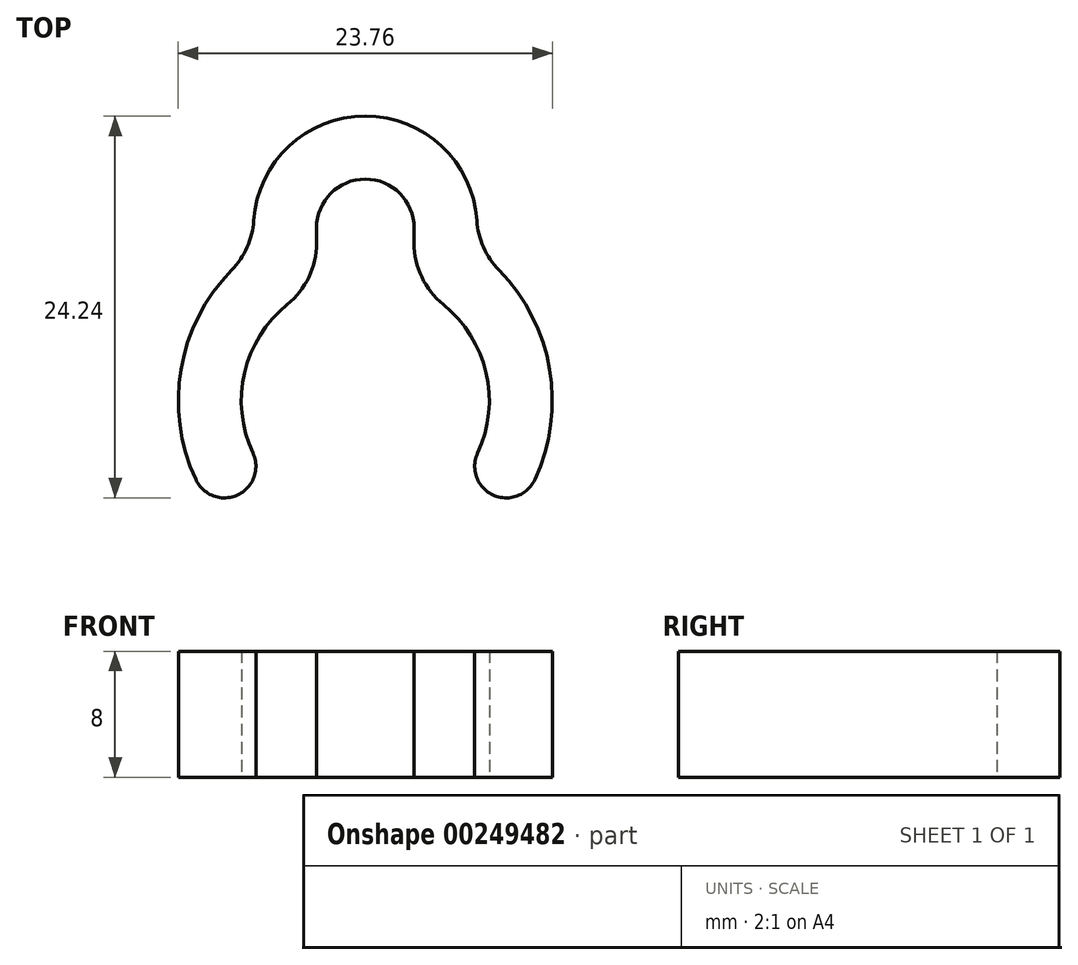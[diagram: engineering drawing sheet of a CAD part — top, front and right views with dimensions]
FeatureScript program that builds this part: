
annotation { "Feature Type Name" : "Feature", "Feature Type Description" : "" }
export const myFeature = defineFeature(function(context is Context, id is Id, definition is map)
    precondition{}
    {
        {
            var Q0;
            Q0=qCreatedBy(makeId("Top.planeOp"),FACE);
            var sketch = newSketch(context, id + "F0", { "sketchPlane" : qUnion([Q0])});
            skCircle(sketch, "E0", {"center": v(0, 0) * mm, "radius": 7.88 * mm, "construction": true});
            skCircle(sketch, "E1", {"center": v(0, 10.97) * mm, "radius": 3.1 * mm, "construction": true});
            skSolve(sketch);
        }
        {
            var Q0;
            Q0=qCreatedBy(makeId("Top.planeOp"),FACE);
            var sketch = newSketch(context, id + "F1", { "sketchPlane" : qUnion([Q0])});
            skArc(sketch, "E2", {"start": v(7.14, -3.33) * mm, "mid": v(7.67, 1.77) * mm, "end": v(4.95, 6.12) * mm});
            skLineSegment(sketch, "E3", {"start": v(0, 0) * mm, "end": v(-7.14, -3.33) * mm, "construction": true});
            skLineSegment(sketch, "E4", {"start": v(0, 0) * mm, "end": v(7.14, -3.33) * mm, "construction": true});
            skArc(sketch, "E5", {"start": v(10.76, -5.02) * mm, "mid": v(11.7, 2) * mm, "end": v(8.5, 8.3) * mm});
            skLineSegment(sketch, "E6", {"start": v(7.14, -3.33) * mm, "end": v(10.76, -5.02) * mm, "construction": true});
            skLineSegment(sketch, "E7", {"start": v(-7.14, -3.33) * mm, "end": v(-10.76, -5.02) * mm, "construction": true});
            skArc(sketch, "E8", {"start": v(-10.76, -5.02) * mm, "mid": v(-8.1, -5.99) * mm, "end": v(-7.14, -3.33) * mm});
            skArc(sketch, "E9", {"start": v(7.14, -3.33) * mm, "mid": v(8.1, -5.99) * mm, "end": v(10.76, -5.02) * mm});
            skArc(sketch, "E10", {"start": v(3.1, 10.97) * mm, "mid": v(0, 14.08) * mm, "end": v(-3.1, 10.97) * mm});
            skLineSegment(sketch, "E11", {"start": v(-3.1, 10.97) * mm, "end": v(-3.1, 10) * mm});
            skLineSegment(sketch, "E12", {"start": v(3.1, 10.97) * mm, "end": v(3.1, 10) * mm});
            skArc(sketch, "E13.trimOffspring", {"start": v(-4.95, 6.12) * mm, "mid": v(-7.67, 1.77) * mm, "end": v(-7.14, -3.33) * mm});
            skArc(sketch, "E14.trimOffspring", {"start": v(-8.5, 8.3) * mm, "mid": v(-11.7, 2) * mm, "end": v(-10.76, -5.02) * mm});
            skArc(sketch, "E15", {"start": v(7.08, 11.45) * mm, "mid": v(0, 18.07) * mm, "end": v(-7.08, 11.45) * mm});
            skPoint(sketch, "E16.visualSharp", {"position": v(-6.97, 9.62) * mm});
            skArc(sketch, "E16.filletArc", {"start": v(-8.5, 8.3) * mm, "mid": v(-7.5, 9.75) * mm, "end": v(-7.08, 11.45) * mm});
            skPoint(sketch, "E17.visualSharp", {"position": v(6.97, 9.62) * mm});
            skArc(sketch, "E17.filletArc", {"start": v(7.08, 11.45) * mm, "mid": v(7.5, 9.75) * mm, "end": v(8.5, 8.3) * mm});
            skPoint(sketch, "E18.visualSharp", {"position": v(3.1, 7.24) * mm});
            skArc(sketch, "E18.filletArc", {"start": v(3.1, 10) * mm, "mid": v(3.59, 7.85) * mm, "end": v(4.95, 6.12) * mm});
            skPoint(sketch, "E19.visualSharp", {"position": v(-3.1, 7.24) * mm});
            skArc(sketch, "E19.filletArc", {"start": v(-4.95, 6.12) * mm, "mid": v(-3.59, 7.85) * mm, "end": v(-3.1, 10) * mm});
            skSolve(sketch);
        }
        {
            var Q0;
            Q0 = qSketchRegion(id + "F1", true);
            extrude(context, id + "F2", {"entities" : qUnion([Q0]), "depth" : 8 * mm});
        }
    });
